# Revit family: 511_CC_nailfin
name_source: partatom
category: Windows
revit_build: Autodesk Revit 2016 (Build: 20150220_1215(x64)
units: mm (PartAtom-declared; Revit-internal decimal feet)

## family parameters
Always vertical = Yes
Cut with Voids When Loaded = No
Host = Wall
OmniClass Number = 23.30.20.00
OmniClass Title = Windows
Room Calculation Point = No
Shared = No

## types (41) — shared parameters
Default Sill Height = 31 1/2"
MLW = 3 1/4"
Wall Closure = By host

## per-type parameters (varying)
| type | Bar set | Height | MLH | Width |
| 72x48 | 36" | 48" | 24" | 72" |
| 27x19.75Min | 13 1/2" | 19 3/4" | 9 7/8" | 27" |
| 60x72Max | 30" | 72" | 36" | 60" |
| 72x60Max | 36" | 60" | 30" | 72" |
| 36x36 | 18" | 36" | 18" | 36" |
| 48x48 | 24" | 48" | 24" | 48" |
| 60x60 | 30" | 60" | 30" | 60" |
| 72x54 | 36" | 54" | 27" | 72" |
| 72x42 | 36" | 42" | 21" | 72" |
| 72x36 | 36" | 36" | 18" | 72" |
| 60x66 | 30" | 66" | 33" | 60" |
| 60x36 | 30" | 36" | 18" | 60" |
| 60x30 | 30" | 30" | 15" | 60" |
| 60x42 | 30" | 42" | 21" | 60" |
| 60x48 | 30" | 48" | 24" | 60" |
| 60x54 | 30" | 54" | 27" | 60" |
| 66x36 | 33" | 36" | 18" | 66" |
| 66x42 | 33" | 42" | 21" | 66" |
| 66x48 | 33" | 48" | 24" | 66" |
| 66x54 | 33" | 54" | 27" | 66" |
| 66x60 | 33" | 60" | 30" | 66" |
| 54x30 | 27" | 30" | 15" | 54" |
| 54x36 | 27" | 36" | 18" | 54" |
| 54x42 | 27" | 42" | 21" | 54" |
| 54x48 | 27" | 48" | 24" | 54" |
| 54x54 | 27" | 54" | 27" | 54" |
| 48x30 | 24" | 30" | 15" | 48" |
| 48x24 | 24" | 24" | 12" | 48" |
| 48x36 | 24" | 36" | 18" | 48" |
| 48x42 | 24" | 42" | 21" | 48" |
| 48x54 | 24" | 54" | 27" | 48" |
| 36x20 | 18" | 20" | 10" | 36" |
| 36x24 | 18" | 24" | 12" | 36" |
| 36x30 | 18" | 30" | 15" | 36" |
| 36x42 | 18" | 42" | 21" | 36" |
| 36x48 | 18" | 48" | 24" | 36" |
| 30x20 | 15" | 20" | 10" | 30" |
| 30x24 | 15" | 24" | 12" | 30" |
| 30x30 | 15" | 30" | 15" | 30" |
| 30x36 | 15" | 36" | 18" | 30" |
| 30x42 | 15" | 42" | 21" | 30" |

## geometry (parser evidence)
native form markers: Sweep x3
no freeform markers — native parametric forms only
